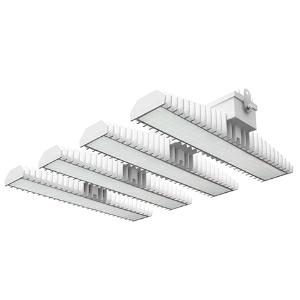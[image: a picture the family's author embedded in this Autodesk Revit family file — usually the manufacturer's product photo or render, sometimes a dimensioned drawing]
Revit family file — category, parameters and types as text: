
# Revit family: 3f_filippi_-_3f_lem_medio_3f_filippi_-_58913_a0812_-_3f_lem_4_led_200_dali_cr_medio___vs_94be
name_source: partatom
category: Lighting Fixtures
units: mm (PartAtom-declared; Revit-internal decimal feet)

## family parameters
Cut with Voids When Loaded = No
Host = Face
Light Source = No
Part Type = Normal
Room Calculation Point = No
Round Connector Dimension = Use Diameter
Shared = No

## types (1)
- 3F Filippi - 3F LEM Medio (1 x LED, 26931 lm, 218 W, 4000 K)
    Apparent Load = 218 VA
    Approval mark = CE
    CIE Flux Codes = 77 92 98 100 100
    Color Rendering = 80
    Color Temperature = 4000 K
    Control Gear = Electronic transformer
    Default Elevation = 1800 mm
    Description = Industrial luminaire with high light output and high luminous efficiency designed with the most innovative technologies for environments with temperature up to 55°C.

ILLUMINOTECHNICAL
Luminous efficiency 100% (DLOR 98%, ULOR 2%).
Initial luminous flux of the luminaire 26931 lm.
Medium distribution with rectangular shape.
Installation Interdistance Transv.D = 0.87 x hu - Long.D = 0.87 x hu.
Tabular UGR (CIE 117 - 4H-8H; S=0.25H; 70/50/20): RUG 21.2 - 21.2.
Beam angle: 58° - 57°.
Luminous efficacy 124 lm/W.
Lifetime (L93/B10): 30000 h. (tq+25°C)
Lifetime (L90/B10): 50000 h. (tq+25°C)
Lifetime (L85/B10): 80000 h. (tq+25°C)
Lifetime (L80/B10): 100000 h. (tq+25°C)
Lifetime (L85/B10): 50000 h. (tq+55°C)
Sudden decreased luminous flux after 50000 hours: 0% (C0).
Photobiological safety in compliance with IEC/TR 62778: RG0 risk exempt, (IEC 62471).
In compliance with IEC/EN 62722-2-1 - IEC/EN 62717 standards.

SOURCE
4 Mid-Power linear LED modules 50W/840.
Energy efficiency class (UE 2019/2020 - UE 2019/2015): C.
CIE 13.3 Colour rendering index: CRI >80 (R9 <50%).
IES TM-30 Fidelity Index: Rf = 84 Rg = 95.
CCT nominal colour temperature 4000 K.
Colour initial tolerance (MacAdam): SDCM 3.

MECHANICAL
Passive modular heatsinks in die-casted aluminium, painted in white colour.
To optimize the thermal management of the LED module, the heatsinks are oversized and provided with self-cleaning of cooling fins.
Wiring body in aluminium and galvanised steel anchored solidly to the sinks and thermally separated.
3F Lens lenses with high luminous efficiency, transparent methacrylate (PMMA), fixed to the LED modules.
Fixing brackets in stainless steel.
Luminaire with limited surface temperature. - D - (EN 60598-2-24)
Dimensions: 757x542 mm, height 133 mm. Weight 18.93 kg.
IP65 protection degree.
Mechanical strength to impacts IK06 (1 joule).
Glow-wire test resistance 650°C.

ELECTRICAL
Halogen Free DALI-2 DATI (Parts 251, 252, 253), PUSH-DIM, electronic wiring 230V-50/60Hz, power factor 0.97 at full load, THD <25%, constant output current, class I, 2 driver, 2 DALI addresses.
Power of the luminaire 218 W.
ENEC - CE.
Flicker: <4%.
Luminaire compliant with EN 60598-2-22 for power supply from a centralised emergency system CPSS (Central Power Supply System), not incorporated in the luminaire - high risk areas excluded. The default power and flux are 100% in AC and 15% in DC.
Ambient temperature from -30°C to +55°C.
Temperature class T6 max 85°C.
Quick connection via M25 5P connector with 9-13 mm tightening range.
Power unit positioned on a separate compartment by the LED module to ensure optimum temperatures of cabling components, to be inspectable and maintainable.
Relative humidity UR: <85%.

INSTALLATION
Ceiling / Suspended / Wall.
All accessories dedicated to this product are available on the Catalog and on our website www.3F-Filippi.com.

ACCESSORIES
A0812 - Anti-glare microprismatic VS moulded glass, tempered, not flammable, with sealing gasket.
One required for each light module. The pack contains 10 pieces.

APPLICATIONS
In commercial environments, exhibition and industrial areas, stores, open areas.
Applications with high ambient temperature up to 55°C.
Environments in which it is necessary a total protection against falling fragments (eg environments with foodstuffs or machines with moving parts or with extreme temperature changes), use luminaires with polycarbonate lenses.

LIGHT MANAGEMENT
Recommended minimum setting: 10%.
The luminaire, equipped with (DALI-2 DATI) driver, can be controlled manually with 3F Easy Dim technology or automatically/manually with wired or wireless DALI/D2D control systems.
The D2D driver guarantees interoperability with other devices with the same certification by making the following information available:
Device Data (Part 251), Energy Report (Part 252), Diagnosis & Maintenance (Part 253).
In electrical systems without a regulation system (manual or automatic) and DALI bus, a suitable jumper must be made on the DA-DA terminals of the appliance.

WARNING
Fixture not suitable for cold stores with an ambient temperature <0°C and/or relative humidity >85%.
Luminaire designed for disposal/recycling at end-of-life.
Replaceable (LED only) light source by a professional. Replaceable control gear by a professional.
    Height = 133 mm  [stored 0.436352 ft]
    Lamp = 1 x LED
    Lamp Light Flux = 26931 lm
    Lamp Power = 218 W
    Lamp count = 1
    Length = 757 mm
    Lifetime = 50000 h
    Luminous efficacy = 124 lm/W
    Manufacturer = 3F Filippi
    ModVariant = No
    Model = 3F Filippi - 58913+A0812 - 3F LEM 4 LED 200 DALI CR MEDIO + VS
    Mounting Place = Ceiling
    Mounting Type = Pendant
    Number of Poles = 1
    OnlyDefault = Yes
    Power Factor = 1
    Product Name = 3F Filippi - 3F LEM Medio
    Product group = pendant luminaire
    ProductGroupID = 9
    Protection Class = Protection class I
    Protection Degree = IP 65
    RLX_Detail_Level = 1
    RLX_Emergency_Light_Flux = 0 lm
    RLX_Emergency_Type = 0
    RLX_Emergency_Type_DB = No
    RlxData = <blob elided: 122477 chars, md5=773adec1>
    Socket = socket
    Standby Power = 0 W
    System Light Flux = 26931 lm
    System Power = 218 W
    Type Comments = Product without accessories
    Type Image = 3f_filippi_-_lem_4__a0812.jpg
    URL = http://relux.com
    VarID = ---
    Voltage = 0 V
    Weight = 0.00 kg
    Width = 542 mm

note: [stored X ft] marks values corroborated as IEEE doubles in the binary element streams (Revit-internal decimal feet)

## geometry (parser evidence)
native form markers: Blend x4, Sweep x11
no freeform markers — native parametric forms only
